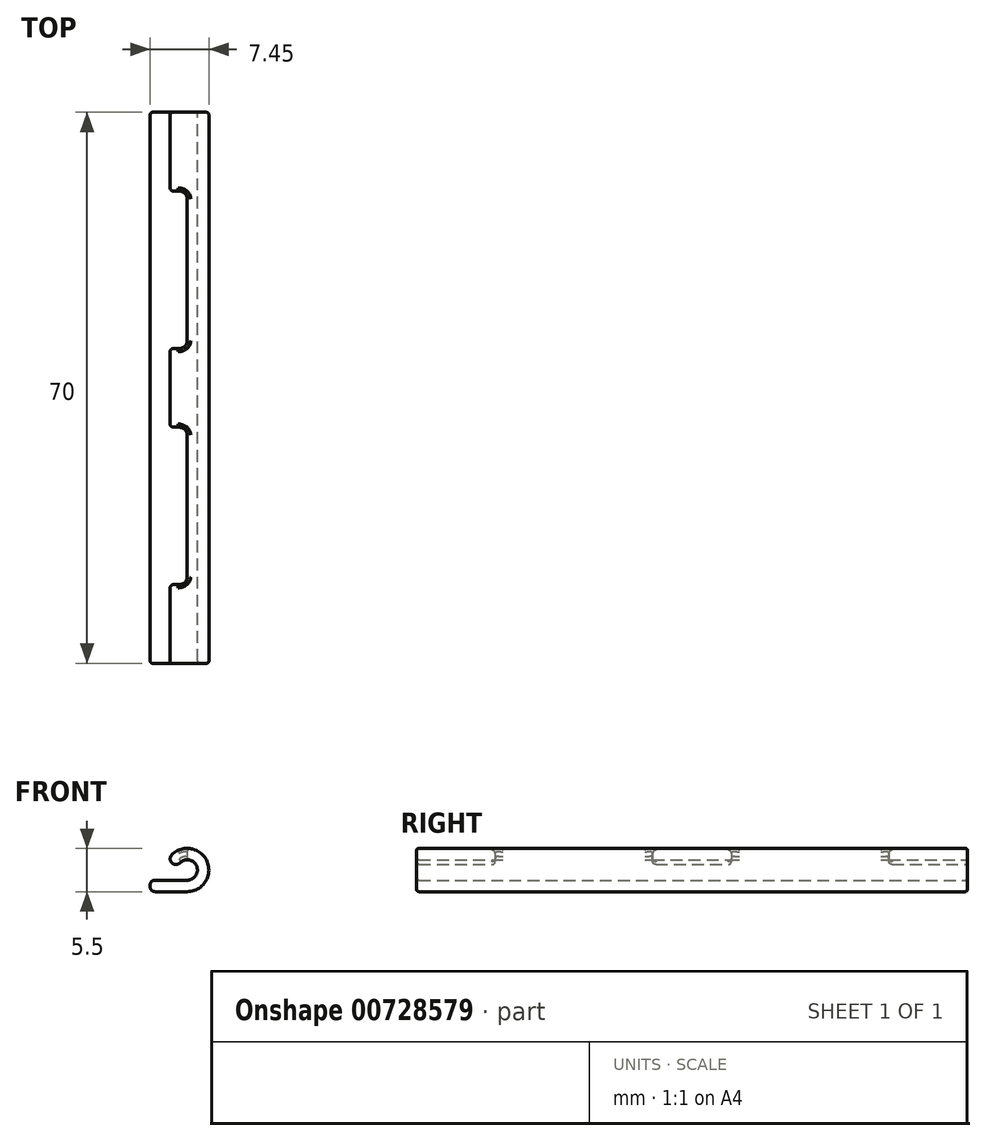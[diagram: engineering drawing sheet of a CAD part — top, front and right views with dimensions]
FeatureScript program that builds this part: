
annotation { "Feature Type Name" : "Feature", "Feature Type Description" : "" }
export const myFeature = defineFeature(function(context is Context, id is Id, definition is map)
    precondition{}
    {
        {
            var Q0;
            Q0=qCreatedBy(makeId("Front.planeOp"),FACE);
            var sketch = newSketch(context, id + "F0", { "sketchPlane" : qUnion([Q0])});
            skArc(sketch, "E0", {"start": v(0, -2.75) * mm, "mid": v(2.54, 1.06) * mm, "end": v(-1.95, 1.94) * mm});
            skArc(sketch, "E1", {"start": v(0, -1.3) * mm, "mid": v(1.2, 0.5) * mm, "end": v(-0.92, 0.91) * mm});
            skLineSegment(sketch, "E2", {"start": v(0, -1.3) * mm, "end": v(-4.1, -1.3) * mm});
            skLineSegment(sketch, "E3", {"start": v(-4.7, -1.9) * mm, "end": v(-4.7, -2.15) * mm});
            skLineSegment(sketch, "E4", {"start": v(-4.1, -2.75) * mm, "end": v(0, -2.75) * mm});
            skArc(sketch, "E5", {"start": v(-1.95, 1.94) * mm, "mid": v(-1.95, 0.9) * mm, "end": v(-0.92, 0.91) * mm});
            skPoint(sketch, "E6.visualSharp", {"position": v(-4.7, -1.3) * mm});
            skArc(sketch, "E6.filletArc", {"start": v(-4.1, -1.3) * mm, "mid": v(-4.52, -1.48) * mm, "end": v(-4.7, -1.9) * mm});
            skPoint(sketch, "E7.visualSharp", {"position": v(-4.7, -2.75) * mm});
            skArc(sketch, "E7.filletArc", {"start": v(-4.7, -2.15) * mm, "mid": v(-4.52, -2.57) * mm, "end": v(-4.1, -2.75) * mm});
            skSolve(sketch);
        }
        {
            var Q0;
            Q0=makeQuery(id+"F0.imprint","IMPRINT",FACE,{"disambiguationData":[TD([[makeQuery(id+"F0.imprint","IMPRINT",EDGE,{"derivedFrom":sQuery(id+"F0.wireOp",EDGE,"E0")}),1.0]])]});
            extrude(context, id + "F1", {"entities" : qUnion([Q0]), "endBound" : BoundingType.SYMMETRIC, "depth" : 70 * mm, "offsetDistance" : 25 * mm});
        }
        {
            var Q0;
            Q0=makeQuery(id+"F1.opExtrude","SWEPT_FACE",FACE,{"disambiguationData":[OSD([sQuery(id+"F0.wireOp",EDGE,"E2")])]});
            var sketch = newSketch(context, id + "F2", { "sketchPlane" : qUnion([Q0])});
            skLineSegment(sketch, "E8", {"start": v(-4.7, 25) * mm, "end": v(0, 25) * mm});
            skLineSegment(sketch, "E9", {"start": v(0, 25) * mm, "end": v(0, 5) * mm});
            skLineSegment(sketch, "E10", {"start": v(0, 5) * mm, "end": v(-4.1, 5) * mm});
            skLineSegment(sketch, "E11", {"start": v(-4.1, 5) * mm, "end": v(-4.1, -5) * mm});
            skLineSegment(sketch, "E12", {"start": v(-4.1, -5) * mm, "end": v(0, -5) * mm});
            skLineSegment(sketch, "E13", {"start": v(0, -5) * mm, "end": v(0, -25) * mm});
            skLineSegment(sketch, "E14", {"start": v(0, -25) * mm, "end": v(-4.7, -25) * mm});
            skLineSegment(sketch, "E15", {"start": v(-4.7, -25) * mm, "end": v(-4.7, 25) * mm});
            skLineSegment(sketch, "E16", {"start": v(-4.1, 0) * mm, "end": v(-21.43, 0) * mm, "construction": true});
            skSolve(sketch);
        }
        {
            var Q0;
            Q0 = qSketchRegion(id + "F2", true);
            extrude(context, id + "F3", {"entities" : qUnion([Q0]), "operationType" : NewBodyOperationType.REMOVE, "depth" : 25 * mm, "offsetDistance" : 25 * mm});
        }
        {
            var Q0;
            Q0=makeQuery(id+"F3.boolean.opBoolean","COPY",EDGE,{"derivedFrom":makeQuery(id+"F3.opExtrude","SWEPT_EDGE",EDGE,{"disambiguationData":[OSD([sQuery(id+"F0.wireOp",EDGE,"E1"),sQuery(id+"F0.wireOp",EDGE,"E2"),sQuery(id+"F2.wireOp",EDGE,"E8"),sQuery(id+"F2.wireOp",EDGE,"E9")])]})});
            var Q1;
            Q1=makeQuery(id+"F3.boolean.opBoolean","COPY",EDGE,{"derivedFrom":makeQuery(id+"F3.opExtrude","SWEPT_EDGE",EDGE,{"disambiguationData":[OSD([sQuery(id+"F0.wireOp",EDGE,"E1"),sQuery(id+"F0.wireOp",EDGE,"E2"),sQuery(id+"F2.wireOp",EDGE,"E9"),sQuery(id+"F2.wireOp",EDGE,"E10")])]})});
            var Q2;
            Q2=makeQuery(id+"F3.boolean.opBoolean","COPY",EDGE,{"derivedFrom":makeQuery(id+"F3.opExtrude","SWEPT_EDGE",EDGE,{"disambiguationData":[OSD([sQuery(id+"F0.wireOp",EDGE,"E1"),sQuery(id+"F0.wireOp",EDGE,"E2"),sQuery(id+"F2.wireOp",EDGE,"E12"),sQuery(id+"F2.wireOp",EDGE,"E13")])]})});
            var Q3;
            Q3=makeQuery(id+"F3.boolean.opBoolean","COPY",EDGE,{"derivedFrom":makeQuery(id+"F3.opExtrude","SWEPT_EDGE",EDGE,{"disambiguationData":[OSD([sQuery(id+"F0.wireOp",EDGE,"E1"),sQuery(id+"F0.wireOp",EDGE,"E2"),sQuery(id+"F2.wireOp",EDGE,"E13"),sQuery(id+"F2.wireOp",EDGE,"E14")])]})});
            fillet(context, id + "F4", {"entities" : qUnion([Q0, Q1, Q2, Q3]), "radius" : 1 * mm, "tangentPropagation" : true, "allowEdgeOverflow" : false});
        }
        {
            var Q0;
            Q0=makeQuery(id+"F3.boolean.opBoolean","INTERSECT",EDGE,{"derivedFrom":[makeQuery(id+"F1.opExtrude","SWEPT_FACE",FACE,{"disambiguationData":[OSD([sQuery(id+"F0.wireOp",EDGE,"E0")])]}),makeQuery(id+"F3.opExtrude","SWEPT_FACE",FACE,{"disambiguationData":[OSD([sQuery(id+"F2.wireOp",EDGE,"E9")])]})]});
            var Q1;
            Q1=makeQuery(id+"F3.boolean.opBoolean","INTERSECT",EDGE,{"derivedFrom":[makeQuery(id+"F1.opExtrude","SWEPT_FACE",FACE,{"disambiguationData":[OSD([sQuery(id+"F0.wireOp",EDGE,"E0")])]}),makeQuery(id+"F3.opExtrude","SWEPT_FACE",FACE,{"disambiguationData":[OSD([sQuery(id+"F2.wireOp",EDGE,"E13")])]})]});
            fillet(context, id + "F5", {"entities" : qUnion([Q0, Q1]), "radius" : 0.4 * mm, "tangentPropagation" : true, "allowEdgeOverflow" : false});
        }
        {
            var Q0;
            Q0=makeQuery(id+"F1.opExtrude","CAP_FACE",FACE,{"disambiguationData":[OSD([sQuery(id+"F0.wireOp",EDGE,"E0"),sQuery(id+"F0.wireOp",EDGE,"E1"),sQuery(id+"F0.wireOp",EDGE,"E2"),sQuery(id+"F0.wireOp",EDGE,"E3"),sQuery(id+"F0.wireOp",EDGE,"E4"),sQuery(id+"F0.wireOp",EDGE,"E5"),sQuery(id+"F0.wireOp",EDGE,"E6.filletArc"),sQuery(id+"F0.wireOp",EDGE,"E7.filletArc")])],"isStart":true});
            var Q1;
            Q1=makeQuery(id+"F1.opExtrude","CAP_FACE",FACE,{"disambiguationData":[OSD([sQuery(id+"F0.wireOp",EDGE,"E0"),sQuery(id+"F0.wireOp",EDGE,"E1"),sQuery(id+"F0.wireOp",EDGE,"E2"),sQuery(id+"F0.wireOp",EDGE,"E3"),sQuery(id+"F0.wireOp",EDGE,"E4"),sQuery(id+"F0.wireOp",EDGE,"E5"),sQuery(id+"F0.wireOp",EDGE,"E6.filletArc"),sQuery(id+"F0.wireOp",EDGE,"E7.filletArc")])],"isStart":false});
            fillet(context, id + "F6", {"entities" : qUnion([Q0, Q1]), "radius" : 0.3 * mm, "tangentPropagation" : true, "allowEdgeOverflow" : false});
        }
    });
